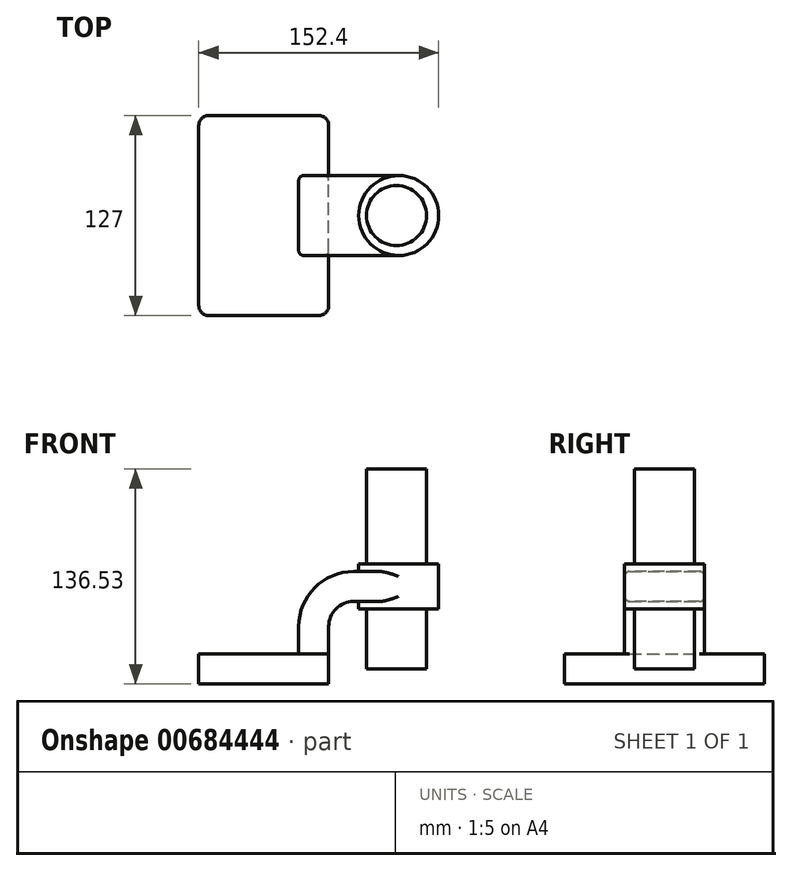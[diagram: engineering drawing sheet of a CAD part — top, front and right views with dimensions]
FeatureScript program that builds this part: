
annotation { "Feature Type Name" : "Feature", "Feature Type Description" : "" }
export const myFeature = defineFeature(function(context is Context, id is Id, definition is map)
    precondition{}
    {
        {
            var Q0;
            Q0=qCreatedBy(makeId("Front.planeOp"),FACE);
            var sketch = newSketch(context, id + "F0", { "sketchPlane" : qUnion([Q0])});
            skLineSegment(sketch, "E0.bottom", {"start": v(-41.28, 9.52) * mm, "end": v(41.28, 9.53) * mm});
            skLineSegment(sketch, "E0.top", {"start": v(-41.28, -9.53) * mm, "end": v(41.28, -9.53) * mm});
            skLineSegment(sketch, "E0.left", {"start": v(-41.28, 9.52) * mm, "end": v(-41.27, -9.53) * mm});
            skLineSegment(sketch, "E0.right", {"start": v(41.28, 9.53) * mm, "end": v(41.28, -9.52) * mm});
            skPoint(sketch, "E0.middle", {"position": v(0, 0) * mm});
            skLineSegment(sketch, "E1.bottom", {"start": v(60.33, 38.1) * mm, "end": v(111.12, 38.1) * mm});
            skLineSegment(sketch, "E1.top", {"start": v(60.33, 66.68) * mm, "end": v(111.12, 66.68) * mm});
            skLineSegment(sketch, "E1.left", {"start": v(60.33, 38.1) * mm, "end": v(60.33, 66.67) * mm});
            skLineSegment(sketch, "E1.right", {"start": v(111.13, 38.1) * mm, "end": v(111.12, 66.67) * mm});
            skPoint(sketch, "E1.middle", {"position": v(85.72, 52.39) * mm});
            skLineSegment(sketch, "E2", {"start": v(41.27, 9.53) * mm, "end": v(41.27, 27) * mm});
            skArc(sketch, "E3", {"start": v(41.27, 27) * mm, "mid": v(45.92, 38.23) * mm, "end": v(57.15, 42.88) * mm});
            skLineSegment(sketch, "E4", {"start": v(57.15, 42.88) * mm, "end": v(85.73, 42.88) * mm});
            skLineSegment(sketch, "E5.0", {"start": v(57.15, 61.93) * mm, "end": v(85.72, 61.93) * mm});
            skArc(sketch, "E5.1", {"start": v(22.22, 27) * mm, "mid": v(32.45, 51.7) * mm, "end": v(57.15, 61.93) * mm});
            skLineSegment(sketch, "E5.2", {"start": v(22.22, 9.53) * mm, "end": v(22.22, 27) * mm});
            skLineSegment(sketch, "E6", {"start": v(85.72, 38.1) * mm, "end": v(85.72, 66.68) * mm});
            skFitSpline(sketch, "E7", {"points": [v(-41.28, 9.52) * mm, v(57.15, 61.93) * mm], "startDerivative": vector(47.8, 119.78) * mm, "endDerivative": vector(158.07, -1.98) * mm});
            skSolve(sketch);
        }
        {
            var Q0;
            Q0=makeQuery(id+"F0.imprint","IMPRINT",FACE,{"disambiguationData":[TD([[makeQuery(id+"F0.imprint","IMPRINT",EDGE,{"derivedFrom":sQuery(id+"F0.wireOp",EDGE,"E0.top")}),1.0]])]});
            var sketch = newSketch(context, id + "F1", { "sketchPlane" : qUnion([Q0])});
            skSolve(sketch);
        }
        {
            var Q0;
            Q0 = qSketchRegion(id + "F1", true);
            var Q1;
            Q1=makeQuery(id+"F0.imprint","IMPRINT",FACE,{"disambiguationData":[TD([[makeQuery(id+"F0.imprint","IMPRINT",EDGE,{"derivedFrom":sQuery(id+"F0.wireOp",EDGE,"E0.top")}),1.0]])]});
            extrude(context, id + "F2", {"entities" : qUnion([Q0, Q1]), "endBound" : BoundingType.SYMMETRIC, "depth" : 127 * mm, "offsetDistance" : 25.4 * mm});
        }
        {
            var Q0;
            {var subQ1=sQuery(id+"F0.wireOp",EDGE,"E2");Q0=makeQuery(id+"F0.imprint","IMPRINT",FACE,{"disambiguationData":[TD([[makeQuery(id+"F0.imprint","IMPRINT",EDGE,{"derivedFrom":subQ1}),1.0]])]});}
            var Q1;
            {var subQ0=sQuery(id+"F0.wireOp",EDGE,"E4");var subQ1=sQuery(id+"F0.wireOp",EDGE,"E1.left");var subQ2=makeQuery(id+"F0.imprint","INTERSECT",VERTEX,{"derivedFrom":[subQ1,subQ0]});Q1=makeQuery(id+"F0.imprint","IMPRINT",FACE,{"disambiguationData":[TD([[makeQuery(id+"F0.imprint","IMPRINT",EDGE,{"disambiguationData":[TD([[subQ2,-1.0]])],"derivedFrom":subQ1}),-1.0]])]});}
            extrude(context, id + "F3", {"entities" : qUnion([Q0, Q1]), "operationType" : NewBodyOperationType.ADD, "endBound" : BoundingType.SYMMETRIC, "depth" : 50.8 * mm, "offsetDistance" : 25.4 * mm});
        }
        {
            var Q0;
            Q0=makeQuery(id+"F0.imprint","IMPRINT",FACE,{"disambiguationData":[TD([[makeQuery(id+"F0.imprint","IMPRINT",EDGE,{"derivedFrom":sQuery(id+"F0.wireOp",EDGE,"E5.1")}),1.0]])]});
            extrude(context, id + "F4", {"entities" : qUnion([Q0]), "operationType" : NewBodyOperationType.ADD, "endBound" : BoundingType.SYMMETRIC, "depth" : 16 * mm, "offsetDistance" : 25.4 * mm});
        }
        {
            var Q0;
            {var subQ0=sQuery(id+"F0.wireOp",EDGE,"E1.right");Q0=makeQuery(id+"F0.imprint","IMPRINT",FACE,{"disambiguationData":[TD([[makeQuery(id+"F0.imprint","IMPRINT",EDGE,{"derivedFrom":subQ0}),1.0]])]});}
            var Q1;
            Q1=sQuery(id+"F0.wireOp",EDGE,"E6");
            revolve(context, id + "F5", {"operationType" : NewBodyOperationType.ADD, "entities" : qUnion([Q0]), "axis" : qUnion([Q1]), "revolveType" : RevolveType.FULL});
        }
        {
            var Q0;
            Q0=makeQuery(id+"F2.opExtrude","CAP_EDGE",EDGE,{"disambiguationData":[OSD([sQuery(id+"F0.wireOp",EDGE,"E0.right")])],"isStart":false});
            var Q1;
            Q1=makeQuery(id+"F2.opExtrude","CAP_EDGE",EDGE,{"disambiguationData":[OSD([sQuery(id+"F0.wireOp",EDGE,"E0.left")])],"isStart":false});
            var Q2;
            Q2=makeQuery(id+"F2.opExtrude","CAP_EDGE",EDGE,{"disambiguationData":[OSD([sQuery(id+"F0.wireOp",EDGE,"E0.right")])],"isStart":true});
            var Q3;
            Q3=makeQuery(id+"F2.opExtrude","CAP_EDGE",EDGE,{"disambiguationData":[OSD([sQuery(id+"F0.wireOp",EDGE,"E0.left")])],"isStart":true});
            fillet(context, id + "F6", {"entities" : qUnion([Q0, Q1, Q2, Q3]), "radius" : 6.35 * mm, "tangentPropagation" : true, "allowEdgeOverflow" : false});
        }
        {
            var Q0;
            Q0=makeQuery(id+"F3.opExtrude","CAP_EDGE",EDGE,{"disambiguationData":[OSD([sQuery(id+"F0.wireOp",EDGE,"E5.1")])],"isStart":false});
            var Q1;
            Q1=makeQuery(id+"F3.opExtrude","CAP_EDGE",EDGE,{"disambiguationData":[OSD([sQuery(id+"F0.wireOp",EDGE,"E5.0")])],"isStart":false});
            var Q2;
            Q2=makeQuery(id+"F3.opExtrude","CAP_EDGE",EDGE,{"disambiguationData":[OSD([sQuery(id+"F0.wireOp",EDGE,"E5.2")])],"isStart":false});
            var Q3;
            Q3=makeQuery(id+"F3.opExtrude","CAP_EDGE",EDGE,{"disambiguationData":[OSD([sQuery(id+"F0.wireOp",EDGE,"E2")])],"isStart":false});
            var Q4;
            Q4=makeQuery(id+"F3.opExtrude","CAP_EDGE",EDGE,{"disambiguationData":[OSD([sQuery(id+"F0.wireOp",EDGE,"E3")])],"isStart":false});
            var Q5;
            Q5=makeQuery(id+"F3.opExtrude","CAP_EDGE",EDGE,{"disambiguationData":[OSD([sQuery(id+"F0.wireOp",EDGE,"E5.2")])],"isStart":true});
            var Q6;
            Q6=makeQuery(id+"F3.opExtrude","CAP_EDGE",EDGE,{"disambiguationData":[OSD([sQuery(id+"F0.wireOp",EDGE,"E5.1")])],"isStart":true});
            var Q7;
            Q7=makeQuery(id+"F3.opExtrude","CAP_EDGE",EDGE,{"disambiguationData":[OSD([sQuery(id+"F0.wireOp",EDGE,"E5.0")])],"isStart":true});
            var Q8;
            Q8=makeQuery(id+"F3.opExtrude","CAP_EDGE",EDGE,{"disambiguationData":[OSD([sQuery(id+"F0.wireOp",EDGE,"E2")])],"isStart":true});
            var Q9;
            Q9=makeQuery(id+"F3.opExtrude","CAP_EDGE",EDGE,{"disambiguationData":[OSD([sQuery(id+"F0.wireOp",EDGE,"E3")])],"isStart":true});
            fillet(context, id + "F7", {"entities" : qUnion([Q0, Q1, Q2, Q3, Q4, Q5, Q6, Q7, Q8, Q9]), "radius" : 3.17 * mm, "tangentPropagation" : true, "allowEdgeOverflow" : false});
        }
        {
            var Q0;
            Q0=qCreatedBy(makeId("Top.planeOp"),FACE);
            var sketch = newSketch(context, id + "F8", { "sketchPlane" : qUnion([Q0])});
            skCircle(sketch, "E8", {"center": v(84.26, 0) * mm, "radius": 19.05 * mm});
            skSolve(sketch);
        }
        {
            var Q0;
            Q0=makeQuery(id+"F8.imprint","IMPRINT",FACE,{"disambiguationData":[TD([[makeQuery(id+"F8.imprint","IMPRINT",EDGE,{"derivedFrom":sQuery(id+"F8.wireOp",EDGE,"E8")}),1.0]])]});
            extrude(context, id + "F9", {"entities" : qUnion([Q0]), "operationType" : NewBodyOperationType.ADD, "depth" : 127 * mm, "offsetDistance" : 25.4 * mm});
        }
    });
